# Revit family: PRD_AR_JntrlSnks_SIRIUSBoot-cleaningUnit_SIRB714_SIRB715
name_source: partatom
category: Specialty Equipment
revit_build: Autodesk Revit 2018 (Build: 20190510_1515(x64)
units: mm (PartAtom-declared; Revit-internal decimal feet)

## family parameters
Always vertical = Yes
Cut with Voids When Loaded = No
OmniClass Number = 23.45.05.14.14.27
OmniClass Title = Service Sinks
Part Type = Normal
Room Calculation Point = No
Round Connector Dimension = Use Diameter
Shared = No
Work Plane-Based = No

## types (2) — shared parameters
AssetType = Fixed
BodyMaterial = PRD_AR_ResinBondedMaterial_Anthracite
Brushes = Hand and sole brushes
Category = Pr_40_20_96_44, Janitorial sinks
Color = anthracite
Description = Boot cleaning unit made of resin-bonded mineral material with smooth, pore-free surface, anthracite color. With height-adjustable feet, galvanized folding grid, manual brush with lever valve, grab handle, sole-cleaning brushes, spray arrays and DN 15 foot valve.
DiameterNominal = 15  [stored 0.0492126 ft]
DrainSize = 100 mm  [stored 0.328084 ft]
DurationUnit = year
Finish = smooth, pore-free
Grid = Hinged
GrossWeight = 42.00 kg
IfcExportAs = IfcSanitaryTerminalType
IfcExportType = SINK
InletSize = G 1/2 B
Manufacturer = KWC Group AG
ManufacturerName = KWC Group AG
ManufacturerURL = www.kwc.com
Material = Mineral material
MaterialCode = Miranit
Mounting = Pedestal
NBSDescription = Janitorial units
NBSReference = 45-35-70/401
NetWeight = 39.90 kg
NominalDepth = 900 mm  [stored 2.95276 ft]
NominalHeight = 1340 mm  [stored 4.39633 ft]
NominalWidth = 600 mm
NumberOfBrushes = 1
NumberOfWashPlaces = 1
OutletSize = DN 100
ProductInformation = https://pim.kwc.com
RearUpstand = No
SinkType = USERDEFINED
Size = 600 x 1340 x 900 mm (W x H x D)
Splashback = No
Sump = Yes
SumpBasket = Included
TapLedge = No
TypeOfMounting = Inset floor mounting
TypeOfUtilitySink = Cleaner sink
URL = www.kwc.com
Uniclass2015Code = Pr_40_20_96_44
Uniclass2015Title = Janitorial sinks
Uniclass2015Version = Products v1.23
Version = 1
WarrantyDurationUnit = year
WasteHolePosition = Center
zero-valued in all types: MountingOffset

## per-type parameters (varying)
| type | BIMObjectName | BowlFinish | DrainerOrStorage | Features | ModelNumber | Name | NumberOfWasteHoles | Overflow | ProductCode | Spillway | TailorMade | WashRiffle |
| SIRB714 | PRD_AR_JanitorialSinks_SIRIUSBoot-cleaningUnit_SIRB714 |  |  | With DN 100 waste outlet unit, sludge bucket and siphon trap. Dimensions 600 x 425-450 x 900 mm (W x H x D) | 2000101080 | SIRIUS Boot-cleaning unit SIRB714 |  |  | 207.0638.407 |  |  |  |
| SIRB715 | PRD_AR_JanitorialSinks_SIRIUSBoot-cleaningUnit_SIRB715 | High polished | No | With DN 100 waste outlet unit and sludge bucket. Dimensions 600 x 425-450 x 900 mm (W x H x D) | 2000101083 | SIRIUS Boot-cleaning unit SIRB715 | 1 | No | 207.0638.408 | No | No | No |

note: column(s) folded — value = type name in every type: Model, ModelReference

note: [stored X ft] marks values corroborated as IEEE doubles in the binary element streams (Revit-internal decimal feet)

## geometry (parser evidence)
native form markers: Sweep x8
no freeform markers — native parametric forms only
